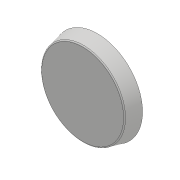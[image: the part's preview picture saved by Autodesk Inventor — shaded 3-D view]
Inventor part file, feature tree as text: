
AUTODESK INVENTOR PART (.ipt)
format: ipt  version: 2017 (Build 210142000, 142)  size: 107,520 bytes
history: native  units: mm
features: fillet x2, revolve x1, shell x1, sketch x1
ambient origin geometry x8: Origin, YZ Plane, XZ Plane, XY Plane, X Axis, Y Axis, Z Axis, Center Point
bodies: Solid1 (feature_tree)
feature tree (5):
  revolve  "Revolution1"  [1 undecoded]
  shell  "Shell1"  Thickness=13.0mm
  fillet  "Fillet1"  [1 undecoded]
  fillet  "Fillet2"  Radius=1.2mm
  sketch  "Sketch1"  dims[d0=13.439035mm d2=37.0mm d3=13.0mm d4=90.0deg d5=1.2mm d6=1.0mm d7=1.0mm]
note: 2 required parameter values undecoded (feature->parameter linkage not recoverable at this tier; creation-order binding heuristic only, values carry confidence <= 0.55)